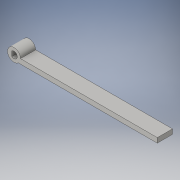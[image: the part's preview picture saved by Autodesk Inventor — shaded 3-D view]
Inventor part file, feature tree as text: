
AUTODESK INVENTOR PART (.ipt)
format: ipt  version: 2016 SP1 (Build 200210100, 210)  size: 104,960 bytes
history: native  units: in
note: dims shown in document units (in); Inventor stores cm internally (conversion verified against a paired STEP export)
features: other x3, sketch x1
ambient origin geometry x8: Origin, YZ Plane, XZ Plane, XY Plane, X Axis, Y Axis, Z Axis, Center Point
bodies: Solid1 (feature_tree)
feature tree (4):
  other  "Rotator2.ipt"
  other  "Solid1::Rotator2.ipt"
  other  "TaggingFeature1"
  sketch  "Sketch1"  dims[d0=0.3937in]
